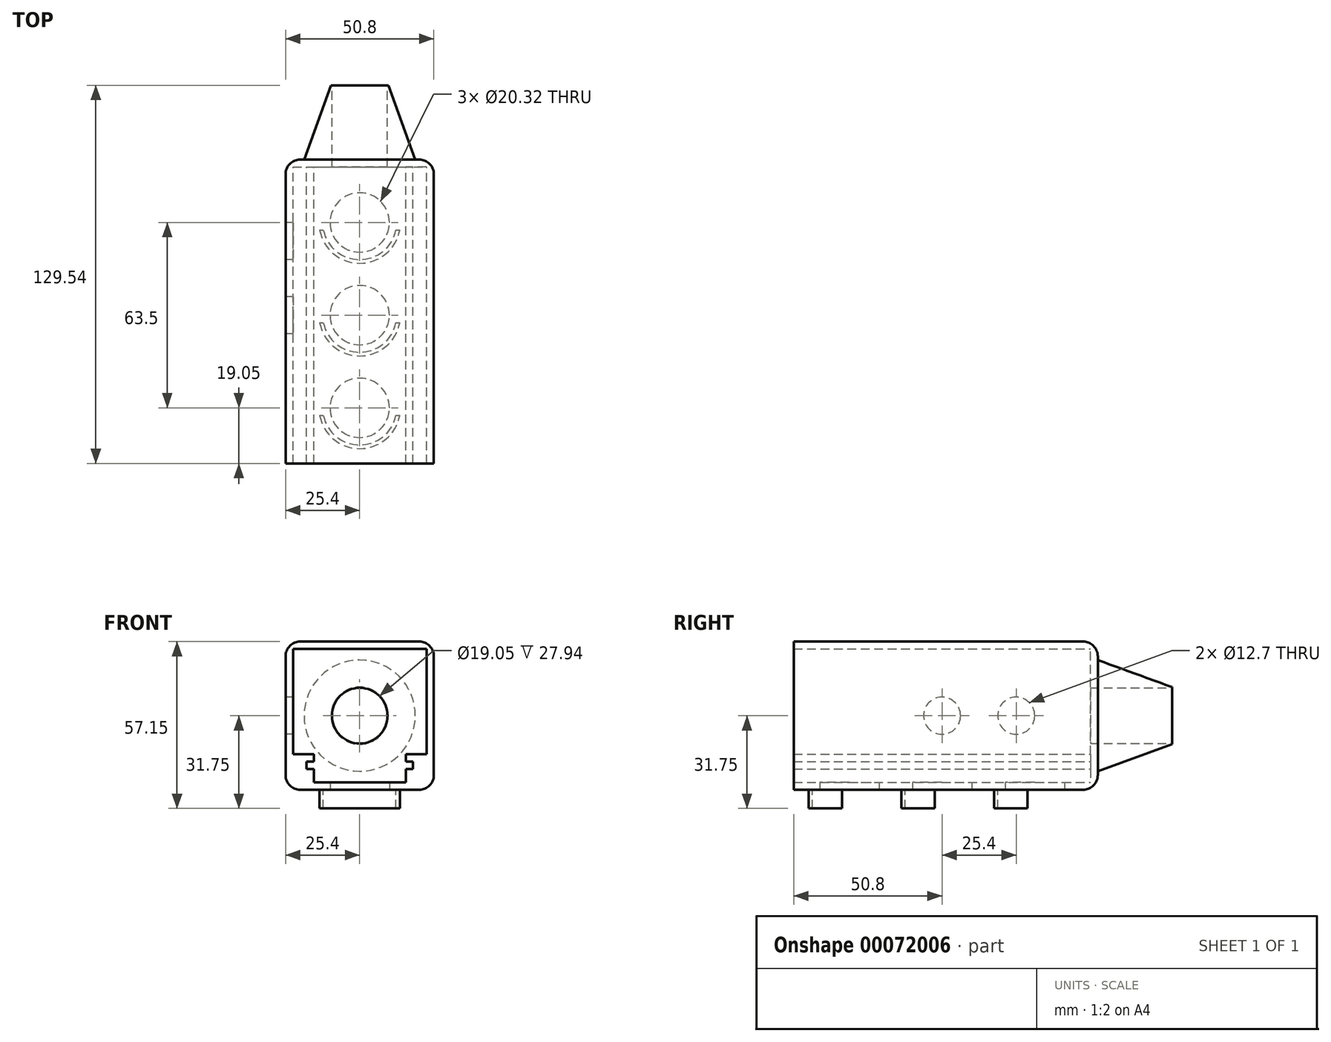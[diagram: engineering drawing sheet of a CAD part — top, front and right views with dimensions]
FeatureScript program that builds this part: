
annotation { "Feature Type Name" : "Feature", "Feature Type Description" : "" }
export const myFeature = defineFeature(function(context is Context, id is Id, definition is map)
    precondition{}
    {
        {
            var Q0;
            Q0=qCreatedBy(makeId("Front.planeOp"),FACE);
            var sketch = newSketch(context, id + "F0", { "sketchPlane" : qUnion([Q0])});
            skLineSegment(sketch, "E0.bottom", {"start": v(0, 0) * mm, "end": v(50.8, 0) * mm});
            skLineSegment(sketch, "E0.top", {"start": v(0, 50.8) * mm, "end": v(50.8, 50.8) * mm});
            skLineSegment(sketch, "E0.left", {"start": v(0, 0) * mm, "end": v(0, 50.8) * mm});
            skLineSegment(sketch, "E0.right", {"start": v(50.8, 0) * mm, "end": v(50.8, 50.8) * mm});
            skLineSegment(sketch, "E1.0", {"start": v(2.54, 48.26) * mm, "end": v(48.26, 48.26) * mm});
            skLineSegment(sketch, "E1.1", {"start": v(2.54, 12.2) * mm, "end": v(2.54, 48.26) * mm});
            skLineSegment(sketch, "E1.2", {"start": v(9.65, 2.54) * mm, "end": v(41.15, 2.54) * mm});
            skLineSegment(sketch, "E1.3", {"start": v(48.26, 12.2) * mm, "end": v(48.26, 48.26) * mm});
            skLineSegment(sketch, "E2", {"start": v(2.54, 12.2) * mm, "end": v(9.65, 12.2) * mm});
            skLineSegment(sketch, "E3", {"start": v(9.65, 12.2) * mm, "end": v(9.65, 9.65) * mm});
            skLineSegment(sketch, "E4", {"start": v(9.65, 9.65) * mm, "end": v(7.11, 9.65) * mm});
            skLineSegment(sketch, "E5", {"start": v(7.11, 9.65) * mm, "end": v(7.11, 7.11) * mm});
            skLineSegment(sketch, "E6", {"start": v(7.11, 7.11) * mm, "end": v(9.65, 7.11) * mm});
            skLineSegment(sketch, "E7", {"start": v(9.65, 7.11) * mm, "end": v(9.65, 2.54) * mm});
            skPoint(sketch, "E7.endSnap0", {"position": v(25.4, 2.54) * mm});
            skLineSegment(sketch, "E8", {"start": v(48.26, 12.2) * mm, "end": v(41.15, 12.2) * mm});
            skLineSegment(sketch, "E9", {"start": v(41.15, 12.2) * mm, "end": v(41.15, 9.65) * mm});
            skLineSegment(sketch, "E10", {"start": v(41.15, 9.65) * mm, "end": v(43.69, 9.65) * mm});
            skLineSegment(sketch, "E11", {"start": v(43.69, 9.65) * mm, "end": v(43.69, 7.11) * mm});
            skLineSegment(sketch, "E12", {"start": v(43.69, 7.11) * mm, "end": v(41.15, 7.11) * mm});
            skLineSegment(sketch, "E13", {"start": v(41.15, 7.11) * mm, "end": v(41.15, 2.54) * mm});
            skPoint(sketch, "E14.orphan", {"position": v(2.54, 2.54) * mm});
            skPoint(sketch, "E15.orphan", {"position": v(48.26, 2.54) * mm});
            skSolve(sketch);
        }
        {
            var Q0;
            Q0 = qSketchRegion(id + "F0", true);
            extrude(context, id + "F1", {"entities" : qUnion([Q0]), "depth" : 101.6 * mm});
        }
        {
            var Q0;
            Q0=makeQuery(id+"F1.opExtrude","SWEPT_FACE",FACE,{"disambiguationData":[OSD([sQuery(id+"F0.wireOp",EDGE,"E0.bottom")])]});
            var sketch = newSketch(context, id + "F2", { "sketchPlane" : qUnion([Q0])});
            skCircle(sketch, "E16", {"center": v(25.4, 19.05) * mm, "radius": 10.16 * mm});
            skCircle(sketch, "E17", {"center": v(25.4, 50.8) * mm, "radius": 10.16 * mm});
            skCircle(sketch, "E18", {"center": v(25.4, 82.55) * mm, "radius": 10.16 * mm});
            skLineSegment(sketch, "E19", {"start": v(25.4, 0) * mm, "end": v(25.4, 101.6) * mm});
            skSolve(sketch);
        }
        {
            var Q0;
            {var subQ0=sQuery(id+"F2.wireOp",EDGE,"E19");var subQ1=sQuery(id+"F2.wireOp",EDGE,"E16");var subQ2=makeQuery(id+"F2.imprint","INTERSECT",VERTEX,{"disambiguationData":[OD(0.0)],"derivedFrom":[subQ1,subQ0]});Q0=makeQuery(id+"F2.imprint","IMPRINT",FACE,{"disambiguationData":[TD([[makeQuery(id+"F2.imprint","IMPRINT",EDGE,{"disambiguationData":[TD([[subQ2,1.0]])],"derivedFrom":subQ1}),1.0]])]});}
            var Q1;
            {var subQ0=sQuery(id+"F2.wireOp",EDGE,"E19");var subQ1=sQuery(id+"F2.wireOp",EDGE,"E16");var subQ2=makeQuery(id+"F2.imprint","INTERSECT",VERTEX,{"disambiguationData":[OD(0.0)],"derivedFrom":[subQ1,subQ0]});Q1=makeQuery(id+"F2.imprint","IMPRINT",FACE,{"disambiguationData":[TD([[makeQuery(id+"F2.imprint","IMPRINT",EDGE,{"disambiguationData":[TD([[subQ2,-1.0]])],"derivedFrom":subQ1}),1.0]])]});}
            var Q2;
            {var subQ0=sQuery(id+"F2.wireOp",EDGE,"E19");var subQ1=sQuery(id+"F2.wireOp",EDGE,"E17");var subQ2=makeQuery(id+"F2.imprint","INTERSECT",VERTEX,{"disambiguationData":[OD(0.0)],"derivedFrom":[subQ1,subQ0]});Q2=makeQuery(id+"F2.imprint","IMPRINT",FACE,{"disambiguationData":[TD([[makeQuery(id+"F2.imprint","IMPRINT",EDGE,{"disambiguationData":[TD([[subQ2,1.0]])],"derivedFrom":subQ1}),1.0]])]});}
            var Q3;
            {var subQ0=sQuery(id+"F2.wireOp",EDGE,"E19");var subQ1=sQuery(id+"F2.wireOp",EDGE,"E17");var subQ2=makeQuery(id+"F2.imprint","INTERSECT",VERTEX,{"disambiguationData":[OD(0.0)],"derivedFrom":[subQ1,subQ0]});Q3=makeQuery(id+"F2.imprint","IMPRINT",FACE,{"disambiguationData":[TD([[makeQuery(id+"F2.imprint","IMPRINT",EDGE,{"disambiguationData":[TD([[subQ2,-1.0]])],"derivedFrom":subQ1}),1.0]])]});}
            var Q4;
            {var subQ0=sQuery(id+"F2.wireOp",EDGE,"E19");var subQ1=sQuery(id+"F2.wireOp",EDGE,"E18");var subQ2=makeQuery(id+"F2.imprint","INTERSECT",VERTEX,{"disambiguationData":[OD(0.0)],"derivedFrom":[subQ1,subQ0]});Q4=makeQuery(id+"F2.imprint","IMPRINT",FACE,{"disambiguationData":[TD([[makeQuery(id+"F2.imprint","IMPRINT",EDGE,{"disambiguationData":[TD([[subQ2,1.0]])],"derivedFrom":subQ1}),1.0]])]});}
            var Q5;
            {var subQ0=sQuery(id+"F2.wireOp",EDGE,"E19");var subQ1=sQuery(id+"F2.wireOp",EDGE,"E18");var subQ2=makeQuery(id+"F2.imprint","INTERSECT",VERTEX,{"disambiguationData":[OD(0.0)],"derivedFrom":[subQ1,subQ0]});Q5=makeQuery(id+"F2.imprint","IMPRINT",FACE,{"disambiguationData":[TD([[makeQuery(id+"F2.imprint","IMPRINT",EDGE,{"disambiguationData":[TD([[subQ2,-1.0]])],"derivedFrom":subQ1}),1.0]])]});}
            extrude(context, id + "F3", {"entities" : qUnion([Q0, Q1, Q2, Q3, Q4, Q5]), "operationType" : NewBodyOperationType.REMOVE, "oppositeDirection" : true, "depth" : 7.62 * mm});
        }
        {
            var Q0;
            Q0=makeQuery(id+"F1.opExtrude","SWEPT_FACE",FACE,{"disambiguationData":[OSD([sQuery(id+"F0.wireOp",EDGE,"E0.left")])]});
            var sketch = newSketch(context, id + "F4", { "sketchPlane" : qUnion([Q0])});
            skCircle(sketch, "E20", {"center": v(50.8, 25.4) * mm, "radius": 6.35 * mm});
            skPoint(sketch, "E20.centerSnap0", {"position": v(101.6, 25.4) * mm});
            skCircle(sketch, "E21", {"center": v(25.4, 25.4) * mm, "radius": 6.35 * mm});
            skLineSegment(sketch, "E22", {"start": v(101.6, 25.4) * mm, "end": v(0, 25.4) * mm});
            skSolve(sketch);
        }
        {
            var Q0;
            Q0 = qSketchRegion(id + "F4", true);
            extrude(context, id + "F5", {"entities" : qUnion([Q0]), "operationType" : NewBodyOperationType.REMOVE, "oppositeDirection" : true, "depth" : 7.62 * mm});
        }
        {
            var Q0;
            Q0=makeQuery(id+"F1.opExtrude","SWEPT_FACE",FACE,{"disambiguationData":[OSD([sQuery(id+"F0.wireOp",EDGE,"E0.bottom")])]});
            var sketch = newSketch(context, id + "F6", { "sketchPlane" : qUnion([Q0])});
            skArc(sketch, "E23", {"start": v(37.84, 85.1) * mm, "mid": v(25.4, 95.25) * mm, "end": v(12.96, 85.1) * mm});
            skArc(sketch, "E24", {"start": v(39.14, 85.1) * mm, "mid": v(25.4, 96.52) * mm, "end": v(11.66, 85.1) * mm});
            skArc(sketch, "E25", {"start": v(37.84, 53.34) * mm, "mid": v(25.4, 63.5) * mm, "end": v(12.96, 53.34) * mm});
            skArc(sketch, "E26", {"start": v(39.14, 53.34) * mm, "mid": v(25.4, 64.77) * mm, "end": v(11.66, 53.34) * mm});
            skArc(sketch, "E27", {"start": v(37.84, 21.6) * mm, "mid": v(25.4, 31.75) * mm, "end": v(12.96, 21.6) * mm});
            skArc(sketch, "E28", {"start": v(39.14, 21.6) * mm, "mid": v(25.4, 33.02) * mm, "end": v(11.66, 21.6) * mm});
            skLineSegment(sketch, "E29", {"start": v(11.66, 21.6) * mm, "end": v(12.96, 21.6) * mm});
            skLineSegment(sketch, "E30.trimOffspring", {"start": v(37.84, 21.6) * mm, "end": v(39.14, 21.6) * mm});
            skLineSegment(sketch, "E31", {"start": v(11.66, 53.34) * mm, "end": v(12.96, 53.34) * mm});
            skLineSegment(sketch, "E32.trimOffspring", {"start": v(37.84, 53.34) * mm, "end": v(39.14, 53.34) * mm});
            skLineSegment(sketch, "E33", {"start": v(11.66, 85.1) * mm, "end": v(12.96, 85.1) * mm});
            skLineSegment(sketch, "E34.trimOffspring", {"start": v(37.84, 85.1) * mm, "end": v(39.14, 85.1) * mm});
            skSolve(sketch);
        }
        {
            var Q0;
            Q0=makeQuery(id+"F6.imprint","IMPRINT",FACE,{"disambiguationData":[TD([[makeQuery(id+"F6.imprint","IMPRINT",EDGE,{"derivedFrom":sQuery(id+"F6.wireOp",EDGE,"E23")}),-1.0]])]});
            var Q1;
            Q1=makeQuery(id+"F6.imprint","IMPRINT",FACE,{"disambiguationData":[TD([[makeQuery(id+"F6.imprint","IMPRINT",EDGE,{"derivedFrom":sQuery(id+"F6.wireOp",EDGE,"E25")}),-1.0]])]});
            var Q2;
            Q2=makeQuery(id+"F6.imprint","IMPRINT",FACE,{"disambiguationData":[TD([[makeQuery(id+"F6.imprint","IMPRINT",EDGE,{"derivedFrom":sQuery(id+"F6.wireOp",EDGE,"E27")}),-1.0]])]});
            extrude(context, id + "F7", {"entities" : qUnion([Q0, Q1, Q2]), "operationType" : NewBodyOperationType.ADD, "depth" : 6.35 * mm});
        }
        {
            var Q0;
            Q0=makeQuery(id+"F1.opExtrude","CAP_FACE",FACE,{"disambiguationData":[OSD([sQuery(id+"F0.wireOp",EDGE,"E0.bottom"),sQuery(id+"F0.wireOp",EDGE,"E0.top"),sQuery(id+"F0.wireOp",EDGE,"E0.left"),sQuery(id+"F0.wireOp",EDGE,"E0.right"),sQuery(id+"F0.wireOp",EDGE,"E1.0"),sQuery(id+"F0.wireOp",EDGE,"E1.1"),sQuery(id+"F0.wireOp",EDGE,"E1.2"),sQuery(id+"F0.wireOp",EDGE,"E1.3"),sQuery(id+"F0.wireOp",EDGE,"E2"),sQuery(id+"F0.wireOp",EDGE,"E3"),sQuery(id+"F0.wireOp",EDGE,"E4"),sQuery(id+"F0.wireOp",EDGE,"E5"),sQuery(id+"F0.wireOp",EDGE,"E6"),sQuery(id+"F0.wireOp",EDGE,"E7"),sQuery(id+"F0.wireOp",EDGE,"E8"),sQuery(id+"F0.wireOp",EDGE,"E9"),sQuery(id+"F0.wireOp",EDGE,"E10"),sQuery(id+"F0.wireOp",EDGE,"E11"),sQuery(id+"F0.wireOp",EDGE,"E12"),sQuery(id+"F0.wireOp",EDGE,"E13")])],"isStart":true});
            var sketch = newSketch(context, id + "F8", { "sketchPlane" : qUnion([Q0])});
            skLineSegment(sketch, "E35.bottom", {"start": v(-50.8, 50.8) * mm, "end": v(0, 50.8) * mm});
            skLineSegment(sketch, "E35.top", {"start": v(-50.8, 0) * mm, "end": v(0, 0) * mm});
            skLineSegment(sketch, "E35.left", {"start": v(-50.8, 50.8) * mm, "end": v(-50.8, 0) * mm});
            skLineSegment(sketch, "E35.right", {"start": v(0, 50.8) * mm, "end": v(0, 0) * mm});
            skSolve(sketch);
        }
        {
            var Q0;
            Q0 = qSketchRegion(id + "F8", true);
            extrude(context, id + "F9", {"entities" : qUnion([Q0]), "operationType" : NewBodyOperationType.ADD, "depth" : 2.54 * mm});
        }
        {
            var Q0;
            Q0=makeQuery(id+"F9.opExtrude","CAP_FACE",FACE,{"disambiguationData":[OSD([sQuery(id+"F8.wireOp",EDGE,"E35.bottom"),sQuery(id+"F8.wireOp",EDGE,"E35.top"),sQuery(id+"F8.wireOp",EDGE,"E35.left"),sQuery(id+"F8.wireOp",EDGE,"E35.right")])],"isStart":false});
            var sketch = newSketch(context, id + "F10", { "sketchPlane" : qUnion([Q0])});
            skCircle(sketch, "E36", {"center": v(-25.4, 25.4) * mm, "radius": 19.05 * mm});
            skLineSegment(sketch, "E37", {"start": v(0, 25.4) * mm, "end": v(-50.8, 25.4) * mm});
            skSolve(sketch);
        }
        {
            var Q0;
            {var subQ0=sQuery(id+"F10.wireOp",EDGE,"E37");var subQ1=sQuery(id+"F10.wireOp",EDGE,"E36");var subQ2=makeQuery(id+"F10.imprint","INTERSECT",VERTEX,{"disambiguationData":[OD(0.0)],"derivedFrom":[subQ1,subQ0]});Q0=makeQuery(id+"F10.imprint","IMPRINT",FACE,{"disambiguationData":[TD([[makeQuery(id+"F10.imprint","IMPRINT",EDGE,{"disambiguationData":[TD([[subQ2,-1.0]])],"derivedFrom":subQ1}),1.0]])]});}
            var Q1;
            {var subQ0=sQuery(id+"F10.wireOp",EDGE,"E37");var subQ1=sQuery(id+"F10.wireOp",EDGE,"E36");var subQ2=makeQuery(id+"F10.imprint","INTERSECT",VERTEX,{"disambiguationData":[OD(0.0)],"derivedFrom":[subQ1,subQ0]});Q1=makeQuery(id+"F10.imprint","IMPRINT",FACE,{"disambiguationData":[TD([[makeQuery(id+"F10.imprint","IMPRINT",EDGE,{"disambiguationData":[TD([[subQ2,1.0]])],"derivedFrom":subQ1}),1.0]])]});}
            extrude(context, id + "F11", {"entities" : qUnion([Q0, Q1]), "operationType" : NewBodyOperationType.ADD, "depth" : 25.4 * mm, "hasDraft" : true, "draftAngle" : 20 * degree, "draftPullDirection" : true});
        }
        {
            var Q0;
            Q0=makeQuery(id+"F11.opExtrude","CAP_FACE",FACE,{"disambiguationData":[OSD([sQuery(id+"F10.wireOp",EDGE,"E36")])],"isStart":false});
            var sketch = newSketch(context, id + "F12", { "sketchPlane" : qUnion([Q0])});
            skCircle(sketch, "E38", {"center": v(-25.4, 25.4) * mm, "radius": 9.53 * mm});
            skSolve(sketch);
        }
        {
            var Q0;
            Q0=makeQuery(id+"F12.imprint","IMPRINT",FACE,{"disambiguationData":[TD([[makeQuery(id+"F12.imprint","IMPRINT",EDGE,{"derivedFrom":sQuery(id+"F12.wireOp",EDGE,"E38")}),1.0]])]});
            extrude(context, id + "F13", {"entities" : qUnion([Q0]), "operationType" : NewBodyOperationType.REMOVE, "endBound" : BoundingType.THROUGH_ALL, "oppositeDirection" : true, "depth" : 50.8 * mm});
        }
        {
            var Q0;
            Q0=makeQuery(id+"F9.opExtrude","CAP_EDGE",EDGE,{"disambiguationData":[OSD([sQuery(id+"F8.wireOp",EDGE,"E35.top")])],"isStart":false});
            var Q1;
            Q1=makeQuery(id+"F9.opExtrude","CAP_EDGE",EDGE,{"disambiguationData":[OSD([sQuery(id+"F8.wireOp",EDGE,"E35.right")])],"isStart":false});
            var Q2;
            Q2=makeQuery(id+"F9.boolean.opBoolean","MERGE",EDGE,{"derivedFrom":[makeQuery(id+"F1.opExtrude","SWEPT_EDGE",EDGE,{"disambiguationData":[OSD([sQuery(id+"F0.wireOp",EDGE,"E0.bottom"),sQuery(id+"F0.wireOp",EDGE,"E0.left")])]}),makeQuery(id+"F9.opExtrude","SWEPT_EDGE",EDGE,{"disambiguationData":[OSD([sQuery(id+"F8.wireOp",EDGE,"E35.top"),sQuery(id+"F8.wireOp",EDGE,"E35.right")])]})]});
            var Q3;
            Q3=makeQuery(id+"F9.boolean.opBoolean","MERGE",EDGE,{"derivedFrom":[makeQuery(id+"F1.opExtrude","SWEPT_EDGE",EDGE,{"disambiguationData":[OSD([sQuery(id+"F0.wireOp",EDGE,"E0.bottom"),sQuery(id+"F0.wireOp",EDGE,"E0.right")])]}),makeQuery(id+"F9.opExtrude","SWEPT_EDGE",EDGE,{"disambiguationData":[OSD([sQuery(id+"F8.wireOp",EDGE,"E35.top"),sQuery(id+"F8.wireOp",EDGE,"E35.left")])]})]});
            var Q4;
            Q4=makeQuery(id+"F9.opExtrude","CAP_EDGE",EDGE,{"disambiguationData":[OSD([sQuery(id+"F8.wireOp",EDGE,"E35.left")])],"isStart":false});
            var Q5;
            Q5=makeQuery(id+"F9.opExtrude","CAP_EDGE",EDGE,{"disambiguationData":[OSD([sQuery(id+"F8.wireOp",EDGE,"E35.bottom")])],"isStart":false});
            var Q6;
            Q6=makeQuery(id+"F9.boolean.opBoolean","MERGE",EDGE,{"derivedFrom":[makeQuery(id+"F1.opExtrude","SWEPT_EDGE",EDGE,{"disambiguationData":[OSD([sQuery(id+"F0.wireOp",EDGE,"E0.top"),sQuery(id+"F0.wireOp",EDGE,"E0.right")])]}),makeQuery(id+"F9.opExtrude","SWEPT_EDGE",EDGE,{"disambiguationData":[OSD([sQuery(id+"F8.wireOp",EDGE,"E35.bottom"),sQuery(id+"F8.wireOp",EDGE,"E35.left")])]})]});
            var Q7;
            Q7=makeQuery(id+"F9.boolean.opBoolean","MERGE",EDGE,{"derivedFrom":[makeQuery(id+"F1.opExtrude","SWEPT_EDGE",EDGE,{"disambiguationData":[OSD([sQuery(id+"F0.wireOp",EDGE,"E0.top"),sQuery(id+"F0.wireOp",EDGE,"E0.left")])]}),makeQuery(id+"F9.opExtrude","SWEPT_EDGE",EDGE,{"disambiguationData":[OSD([sQuery(id+"F8.wireOp",EDGE,"E35.bottom"),sQuery(id+"F8.wireOp",EDGE,"E35.right")])]})]});
            fillet(context, id + "F14", {"entities" : qUnion([Q0, Q1, Q2, Q3, Q4, Q5, Q6, Q7]), "radius" : 5.08 * mm, "tangentPropagation" : true, "allowEdgeOverflow" : false});
        }
    });
